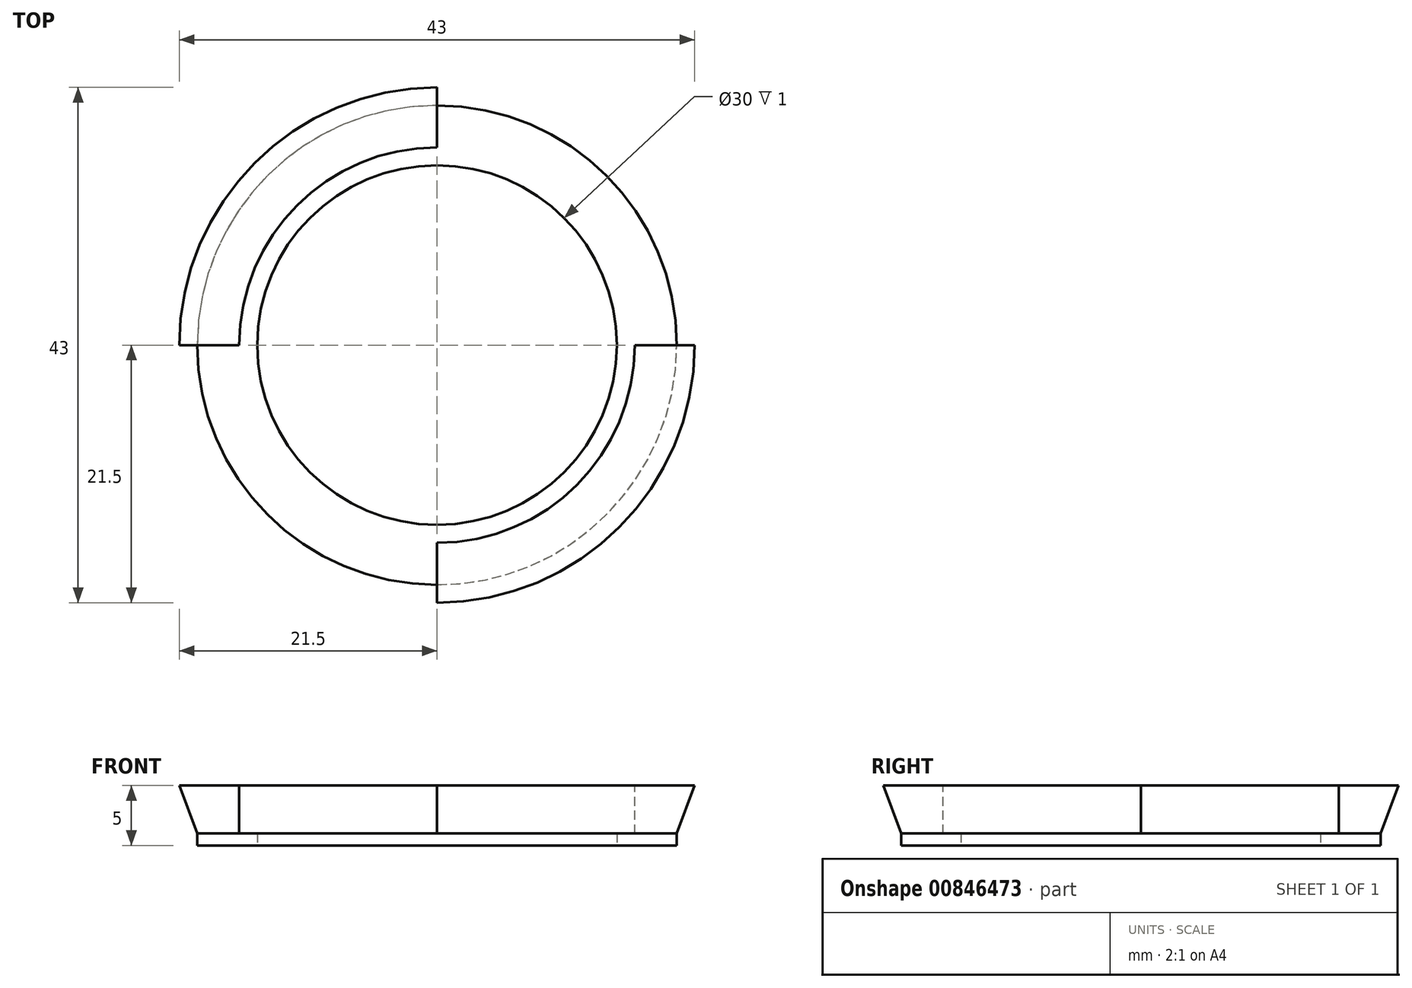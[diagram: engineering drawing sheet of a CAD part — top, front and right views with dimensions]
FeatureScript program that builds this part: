
annotation { "Feature Type Name" : "Feature", "Feature Type Description" : "" }
export const myFeature = defineFeature(function(context is Context, id is Id, definition is map)
    precondition{}
    {
        {
            var Q0;
            Q0=qCreatedBy(makeId("Right.planeOp"),FACE);
            var sketch = newSketch(context, id + "F0", { "sketchPlane" : qUnion([Q0])});
            skLineSegment(sketch, "E0", {"start": v(0, -8.36) * mm, "end": v(0, 5.96) * mm});
            skLineSegment(sketch, "E1", {"start": v(15, 0) * mm, "end": v(15, 1) * mm});
            skLineSegment(sketch, "E2", {"start": v(15, 1) * mm, "end": v(16.5, 1) * mm});
            skLineSegment(sketch, "E3", {"start": v(16.5, 1) * mm, "end": v(16.5, 5) * mm});
            skLineSegment(sketch, "E4", {"start": v(16.5, 5) * mm, "end": v(21.5, 5) * mm});
            skLineSegment(sketch, "E5", {"start": v(21.5, 5) * mm, "end": v(20, 1) * mm});
            skLineSegment(sketch, "E6", {"start": v(20, 1) * mm, "end": v(20, 0) * mm});
            skLineSegment(sketch, "E7", {"start": v(20, 0) * mm, "end": v(15, 0) * mm});
            skSolve(sketch);
        }
        {
            var Q0;
            Q0=makeQuery(id+"F0.imprint","IMPRINT",FACE,{"disambiguationData":[TD([[makeQuery(id+"F0.imprint","IMPRINT",EDGE,{"derivedFrom":sQuery(id+"F0.wireOp",EDGE,"E1")}),-1.0]])]});
            var Q1;
            Q1=sQuery(id+"F0.wireOp",EDGE,"E0");
            revolve(context, id + "F1", {"surfaceOperationType" : NewSurfaceOperationType.NEW, "entities" : qUnion([Q0]), "axis" : qUnion([Q1]), "revolveType" : RevolveType.FULL});
        }
        {
            var Q0;
            Q0=makeQuery(id+"F1.opRevolve","SWEPT_FACE",FACE,{"disambiguationData":[OSD([sQuery(id+"F0.wireOp",EDGE,"E4")])]});
            var sketch = newSketch(context, id + "F2", { "sketchPlane" : qUnion([Q0])});
            skArc(sketch, "E8", {"start": v(0, -16.5) * mm, "mid": v(-11.67, -11.67) * mm, "end": v(-16.5, 0) * mm});
            skArc(sketch, "E9", {"start": v(0, 16.5) * mm, "mid": v(11.67, 11.67) * mm, "end": v(16.5, 0) * mm});
            skLineSegment(sketch, "E10", {"start": v(0, 16.5) * mm, "end": v(0, 21.5) * mm});
            skLineSegment(sketch, "E11", {"start": v(16.5, 0) * mm, "end": v(21.5, 0) * mm});
            skLineSegment(sketch, "E12", {"start": v(-16.5, 0) * mm, "end": v(-21.5, 0) * mm});
            skLineSegment(sketch, "E13", {"start": v(0, -16.5) * mm, "end": v(0, -21.5) * mm});
            skArc(sketch, "E14", {"start": v(0, 21.5) * mm, "mid": v(15.2, 15.2) * mm, "end": v(21.5, 0) * mm});
            skArc(sketch, "E15", {"start": v(-21.5, 0) * mm, "mid": v(-15.2, -15.2) * mm, "end": v(0, -21.5) * mm});
            skSolve(sketch);
        }
        {
            var Q0;
            Q0 = qSketchRegion(id + "F2", true);
            extrude(context, id + "F3", {"entities" : qUnion([Q0]), "operationType" : NewBodyOperationType.REMOVE, "oppositeDirection" : true, "depth" : 4 * mm, "offsetDistance" : 25 * mm});
        }
    });
